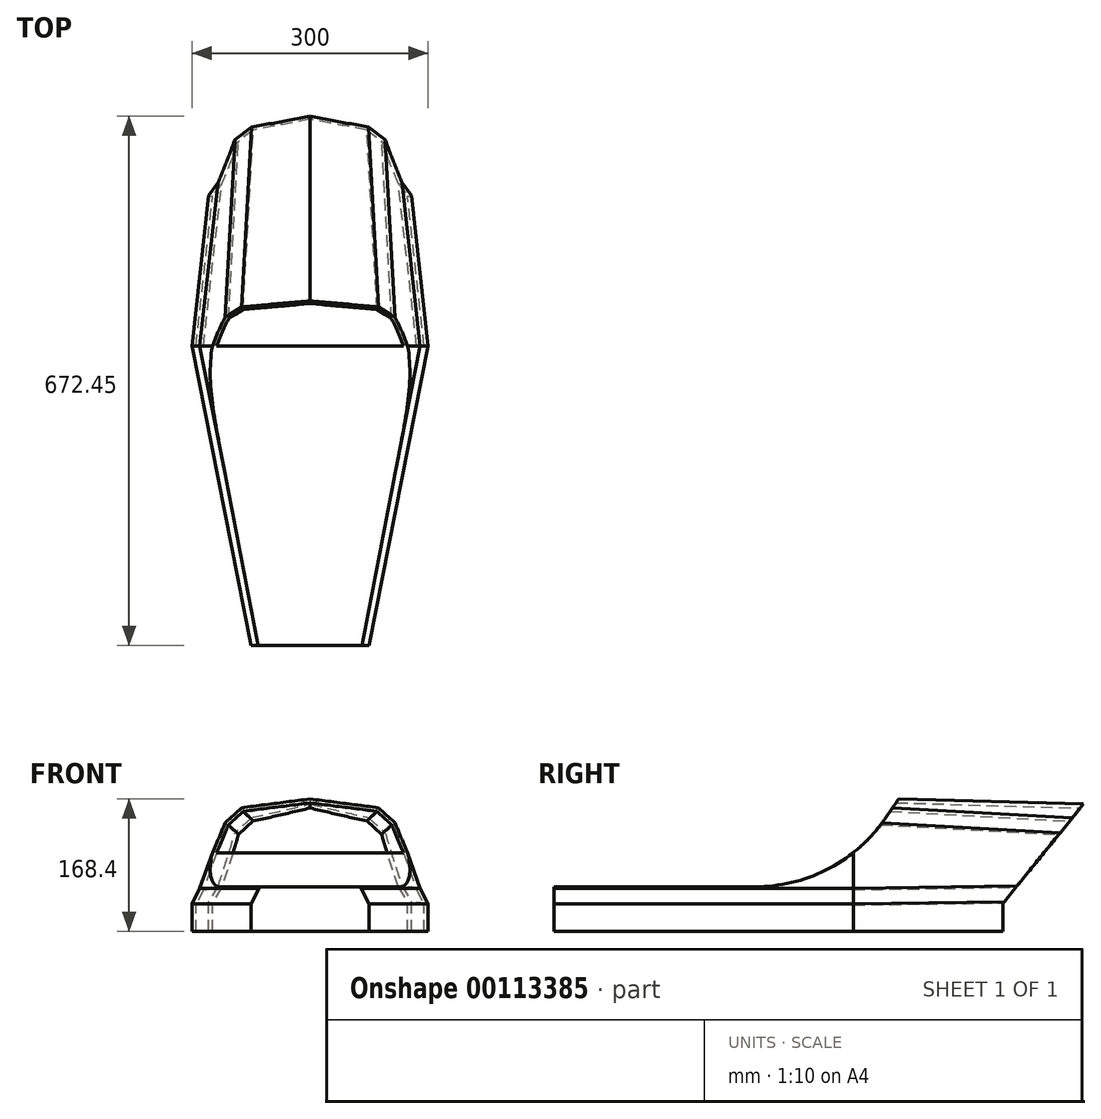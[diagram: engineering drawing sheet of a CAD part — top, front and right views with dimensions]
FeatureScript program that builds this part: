
annotation { "Feature Type Name" : "Feature", "Feature Type Description" : "" }
export const myFeature = defineFeature(function(context is Context, id is Id, definition is map)
    precondition{}
    {
        {
            var Q0;
            Q0=qCreatedBy(makeId("Front.planeOp"),FACE);
            cPlane(context, id + "F0", {"entities" : qUnion([Q0]), "cplaneType" : CPlaneType.OFFSET, "offset" : 360 * mm, "oppositeDirection" : true, "width" : 150 * mm, "height" : 150 * mm});
        }
        {
            var Q0;
            Q0=qCreatedBy(makeId("Front.planeOp"),FACE);
            cPlane(context, id + "F1", {"entities" : qUnion([Q0]), "cplaneType" : CPlaneType.OFFSET, "offset" : 380 * mm, "width" : 150 * mm, "height" : 150 * mm});
        }
        {
            var Q0;
            Q0=qCreatedBy(makeId("Front.planeOp"),FACE);
            var sketch = newSketch(context, id + "F2", { "sketchPlane" : qUnion([Q0])});
            skLineSegment(sketch, "E0", {"start": v(0, 0) * mm, "end": v(0, 170) * mm, "construction": true});
            skLineSegment(sketch, "E1", {"start": v(0, 0) * mm, "end": v(150, 0) * mm, "construction": true});
            skLineSegment(sketch, "E2", {"start": v(150, 0) * mm, "end": v(150, 35) * mm});
            skLineSegment(sketch, "E3", {"start": v(150, 35) * mm, "end": v(140, 35) * mm, "construction": true});
            skLineSegment(sketch, "E4", {"start": v(140, 35) * mm, "end": v(140, 55) * mm, "construction": true});
            skLineSegment(sketch, "E5", {"start": v(0, 170) * mm, "end": v(90, 170) * mm, "construction": true});
            skLineSegment(sketch, "E6", {"start": v(90, 170) * mm, "end": v(90, 160) * mm, "construction": true});
            skLineSegment(sketch, "E7", {"start": v(90, 160) * mm, "end": v(90, 140) * mm, "construction": true});
            skLineSegment(sketch, "E8", {"start": v(90, 140) * mm, "end": v(110, 140) * mm, "construction": true});
            skLineSegment(sketch, "E9", {"start": v(0, 170) * mm, "end": v(90, 160) * mm});
            skLineSegment(sketch, "E10", {"start": v(90, 160) * mm, "end": v(110, 140) * mm});
            skLineSegment(sketch, "E11", {"start": v(110, 140) * mm, "end": v(140, 55) * mm});
            skLineSegment(sketch, "E12", {"start": v(140, 55) * mm, "end": v(150, 35) * mm});
            skLineSegment(sketch, "E13.MirrorCS", {"start": v(-150, 0) * mm, "end": v(-150, 35) * mm});
            skLineSegment(sketch, "E14.MirrorCS", {"start": v(-140, 55) * mm, "end": v(-150, 35) * mm});
            skLineSegment(sketch, "E15.MirrorCS", {"start": v(-110, 140) * mm, "end": v(-140, 55) * mm});
            skLineSegment(sketch, "E16.MirrorCS", {"start": v(0, 170) * mm, "end": v(-90, 160) * mm});
            skLineSegment(sketch, "E17.MirrorCS", {"start": v(-90, 160) * mm, "end": v(-110, 140) * mm});
            skLineSegment(sketch, "E18.0", {"start": v(145, 0) * mm, "end": v(145, 33.82) * mm});
            skLineSegment(sketch, "E18.1", {"start": v(135.39, 53.04) * mm, "end": v(145, 33.82) * mm});
            skLineSegment(sketch, "E18.2", {"start": v(105.66, 137.27) * mm, "end": v(135.39, 53.04) * mm});
            skLineSegment(sketch, "E18.3", {"start": v(87.7, 155.22) * mm, "end": v(105.66, 137.27) * mm});
            skLineSegment(sketch, "E18.4", {"start": v(0, 164.97) * mm, "end": v(87.7, 155.22) * mm});
            skLineSegment(sketch, "E18.5", {"start": v(0, 164.97) * mm, "end": v(-87.7, 155.22) * mm});
            skLineSegment(sketch, "E18.6", {"start": v(-145, 0) * mm, "end": v(-145, 33.82) * mm});
            skLineSegment(sketch, "E18.7", {"start": v(-135.39, 53.04) * mm, "end": v(-145, 33.82) * mm});
            skLineSegment(sketch, "E18.8", {"start": v(-105.66, 137.27) * mm, "end": v(-135.39, 53.04) * mm});
            skLineSegment(sketch, "E18.9", {"start": v(-87.7, 155.22) * mm, "end": v(-105.66, 137.27) * mm});
            skLineSegment(sketch, "E19", {"start": v(-150, 0) * mm, "end": v(-145, 0) * mm});
            skLineSegment(sketch, "E20", {"start": v(145, 0) * mm, "end": v(150, 0) * mm});
            skSolve(sketch);
        }
        {
            var Q0;
            Q0=qCreatedBy(id+"F0.planeOp",FACE);
            var sketch = newSketch(context, id + "F3", { "sketchPlane" : qUnion([Q0])});
            skLineSegment(sketch, "E21", {"start": v(0, 0) * mm, "end": v(0, 160) * mm, "construction": true});
            skLineSegment(sketch, "E22", {"start": v(0, 0) * mm, "end": v(110, 0) * mm, "construction": true});
            skLineSegment(sketch, "E23", {"start": v(110, 0) * mm, "end": v(110, 40) * mm});
            skLineSegment(sketch, "E24", {"start": v(110, 40) * mm, "end": v(100, 40) * mm, "construction": true});
            skLineSegment(sketch, "E25", {"start": v(100, 40) * mm, "end": v(100, 60) * mm, "construction": true});
            skLineSegment(sketch, "E26", {"start": v(0, 160) * mm, "end": v(70, 160) * mm, "construction": true});
            skLineSegment(sketch, "E27", {"start": v(70, 160) * mm, "end": v(70, 140) * mm, "construction": true});
            skLineSegment(sketch, "E28", {"start": v(70, 140) * mm, "end": v(70, 120) * mm, "construction": true});
            skLineSegment(sketch, "E29", {"start": v(70, 120) * mm, "end": v(90, 120) * mm, "construction": true});
            skLineSegment(sketch, "E30", {"start": v(0, 160) * mm, "end": v(70, 140) * mm});
            skLineSegment(sketch, "E31", {"start": v(70, 140) * mm, "end": v(90, 120) * mm});
            skLineSegment(sketch, "E32", {"start": v(90, 120) * mm, "end": v(100, 60) * mm});
            skLineSegment(sketch, "E33", {"start": v(100, 60) * mm, "end": v(110, 40) * mm});
            skLineSegment(sketch, "E34.MirrorCS", {"start": v(-110, 0) * mm, "end": v(-110, 40) * mm});
            skLineSegment(sketch, "E35.MirrorCS", {"start": v(-100, 60) * mm, "end": v(-110, 40) * mm});
            skLineSegment(sketch, "E36.MirrorCS", {"start": v(-90, 120) * mm, "end": v(-100, 60) * mm});
            skLineSegment(sketch, "E37.MirrorCS", {"start": v(0, 160) * mm, "end": v(-70, 140) * mm});
            skLineSegment(sketch, "E38.MirrorCS", {"start": v(-70, 140) * mm, "end": v(-90, 120) * mm});
            skLineSegment(sketch, "E39.0", {"start": v(105, 0) * mm, "end": v(105, 38.82) * mm});
            skLineSegment(sketch, "E39.1", {"start": v(95.2, 58.44) * mm, "end": v(105, 38.82) * mm});
            skLineSegment(sketch, "E39.2", {"start": v(85.33, 117.6) * mm, "end": v(95.2, 58.44) * mm});
            skLineSegment(sketch, "E39.3", {"start": v(67.38, 135.55) * mm, "end": v(85.33, 117.6) * mm});
            skLineSegment(sketch, "E39.4", {"start": v(0, 154.8) * mm, "end": v(67.38, 135.55) * mm});
            skLineSegment(sketch, "E39.5", {"start": v(0, 154.8) * mm, "end": v(-67.38, 135.55) * mm});
            skLineSegment(sketch, "E39.6", {"start": v(-105, 0) * mm, "end": v(-105, 38.82) * mm});
            skLineSegment(sketch, "E39.7", {"start": v(-95.2, 58.44) * mm, "end": v(-105, 38.82) * mm});
            skLineSegment(sketch, "E39.8", {"start": v(-85.33, 117.6) * mm, "end": v(-95.2, 58.44) * mm});
            skLineSegment(sketch, "E39.9", {"start": v(-67.38, 135.55) * mm, "end": v(-85.33, 117.6) * mm});
            skLineSegment(sketch, "E40", {"start": v(-110, 0) * mm, "end": v(-105, 0) * mm});
            skLineSegment(sketch, "E41", {"start": v(110, 0) * mm, "end": v(105, 0) * mm});
            skSolve(sketch);
        }
        {
            var Q0;
            Q0=makeQuery(id+"F2.imprint","IMPRINT",FACE,{"disambiguationData":[TD([[makeQuery(id+"F2.imprint","IMPRINT",EDGE,{"derivedFrom":sQuery(id+"F2.wireOp",EDGE,"E2")}),1.0]])]});
            var Q1;
            Q1=makeQuery(id+"F3.imprint","IMPRINT",FACE,{"disambiguationData":[TD([[makeQuery(id+"F3.imprint","IMPRINT",EDGE,{"derivedFrom":sQuery(id+"F3.wireOp",EDGE,"E23")}),1.0]])]});
            loft(context, id + "F4", {"sheetProfilesArray" : [{ "sheetProfileEntities" : qUnion([Q0]) }, { "sheetProfileEntities" : qUnion([Q1]) }]});
        }
        {
            var Q0;
            Q0=qCreatedBy(makeId("Right.planeOp"),FACE);
            var sketch = newSketch(context, id + "F5", { "sketchPlane" : qUnion([Q0])});
            skLineSegment(sketch, "E42", {"start": v(0, 0) * mm, "end": v(190, 0) * mm, "construction": true});
            skLineSegment(sketch, "E43", {"start": v(190, 0) * mm, "end": v(190, 35.57) * mm});
            skLineSegment(sketch, "E44", {"start": v(190, 35.57) * mm, "end": v(299.22, 170.23) * mm});
            skLineSegment(sketch, "E45", {"start": v(299.22, 170.23) * mm, "end": v(363.76, 190.56) * mm});
            skLineSegment(sketch, "E46", {"start": v(363.76, 190.56) * mm, "end": v(429.83, 105.19) * mm});
            skLineSegment(sketch, "E47", {"start": v(429.83, 105.19) * mm, "end": v(427.62, -24.65) * mm});
            skLineSegment(sketch, "E48", {"start": v(427.62, -24.65) * mm, "end": v(17.26, -21.49) * mm});
            skLineSegment(sketch, "E49", {"start": v(17.26, -21.49) * mm, "end": v(189.97, -2.04) * mm});
            skLineSegment(sketch, "E50", {"start": v(189.97, -2.04) * mm, "end": v(190, 0) * mm});
            skSolve(sketch);
        }
        {
            var Q0;
            Q0=makeQuery(id+"F5.imprint","IMPRINT",FACE,{"disambiguationData":[TD([[makeQuery(id+"F5.imprint","IMPRINT",EDGE,{"derivedFrom":sQuery(id+"F5.wireOp",EDGE,"Y5QNh29d-IWdV-9vjP-PHoZ-EMxwuHQiGpys")}),-1.0]])]});
            var Q1;
            Q1=makeQuery(id+"F5.imprint","IMPRINT",FACE,{"disambiguationData":[TD([[makeQuery(id+"F5.imprint","IMPRINT",EDGE,{"derivedFrom":sQuery(id+"F5.wireOp",EDGE,"E43")}),-1.0]])]});
            extrude(context, id + "F6", {"entities" : qUnion([Q0, Q1]), "operationType" : NewBodyOperationType.REMOVE, "endBound" : BoundingType.SYMMETRIC, "depth" : 300 * mm});
        }
        {
            var Q0;
            Q0=qCreatedBy(id+"F1.planeOp",FACE);
            var sketch = newSketch(context, id + "F7", { "sketchPlane" : qUnion([Q0])});
            skLineSegment(sketch, "E51", {"start": v(0, 0) * mm, "end": v(0, 160) * mm, "construction": true});
            skLineSegment(sketch, "E52", {"start": v(0, 0) * mm, "end": v(75, 0) * mm, "construction": true});
            skLineSegment(sketch, "E53", {"start": v(75, 0) * mm, "end": v(75, 35) * mm});
            skLineSegment(sketch, "E54", {"start": v(75, 35) * mm, "end": v(65, 35) * mm, "construction": true});
            skLineSegment(sketch, "E55", {"start": v(65, 35) * mm, "end": v(65, 55) * mm, "construction": true});
            skLineSegment(sketch, "E56", {"start": v(0, 160) * mm, "end": v(90, 160) * mm, "construction": true});
            skLineSegment(sketch, "E57", {"start": v(90, 160) * mm, "end": v(90, 150) * mm, "construction": true});
            skLineSegment(sketch, "E58", {"start": v(90, 150) * mm, "end": v(90, 130) * mm, "construction": true});
            skLineSegment(sketch, "E59", {"start": v(90, 130) * mm, "end": v(110, 130) * mm, "construction": true});
            skLineSegment(sketch, "E60", {"start": v(0, 160) * mm, "end": v(90, 150) * mm});
            skLineSegment(sketch, "E61", {"start": v(90, 150) * mm, "end": v(110, 130) * mm});
            skLineSegment(sketch, "E62", {"start": v(110, 130) * mm, "end": v(65, 55) * mm});
            skLineSegment(sketch, "E63", {"start": v(65, 55) * mm, "end": v(75, 35) * mm});
            skLineSegment(sketch, "E64.MirrorCS", {"start": v(-75, 0) * mm, "end": v(-75, 35) * mm});
            skLineSegment(sketch, "E65.MirrorCS", {"start": v(-65, 55) * mm, "end": v(-75, 35) * mm});
            skLineSegment(sketch, "E66.MirrorCS", {"start": v(-110, 130) * mm, "end": v(-65, 55) * mm});
            skLineSegment(sketch, "E67.MirrorCS", {"start": v(0, 160) * mm, "end": v(-90, 150) * mm});
            skLineSegment(sketch, "E68.MirrorCS", {"start": v(-90, 150) * mm, "end": v(-110, 130) * mm});
            skLineSegment(sketch, "E69", {"start": v(-75, 0) * mm, "end": v(75, 0) * mm});
            skSolve(sketch);
        }
        {
            var Q0;
            Q0=qCreatedBy(makeId("Front.planeOp"),FACE);
            var sketch = newSketch(context, id + "F8", { "sketchPlane" : qUnion([Q0])});
            skLineSegment(sketch, "E70", {"start": v(0, 0) * mm, "end": v(0, 170) * mm, "construction": true});
            skLineSegment(sketch, "E71", {"start": v(0, 0) * mm, "end": v(150, 0) * mm, "construction": true});
            skLineSegment(sketch, "E72", {"start": v(150, 0) * mm, "end": v(150, 35) * mm});
            skLineSegment(sketch, "E73", {"start": v(150, 35) * mm, "end": v(140, 35) * mm, "construction": true});
            skLineSegment(sketch, "E74", {"start": v(140, 35) * mm, "end": v(140, 55) * mm, "construction": true});
            skLineSegment(sketch, "E75", {"start": v(0, 170) * mm, "end": v(90, 170) * mm, "construction": true});
            skLineSegment(sketch, "E76", {"start": v(90, 170) * mm, "end": v(90, 160) * mm, "construction": true});
            skLineSegment(sketch, "E77", {"start": v(90, 160) * mm, "end": v(90, 140) * mm, "construction": true});
            skLineSegment(sketch, "E78", {"start": v(90, 140) * mm, "end": v(110, 140) * mm, "construction": true});
            skLineSegment(sketch, "E79", {"start": v(0, 170) * mm, "end": v(90, 160) * mm});
            skLineSegment(sketch, "E80", {"start": v(90, 160) * mm, "end": v(110, 140) * mm});
            skLineSegment(sketch, "E81", {"start": v(110, 140) * mm, "end": v(140, 55) * mm});
            skLineSegment(sketch, "E82", {"start": v(140, 55) * mm, "end": v(150, 35) * mm});
            skLineSegment(sketch, "E83.MirrorCS", {"start": v(-150, 0) * mm, "end": v(-150, 35) * mm});
            skLineSegment(sketch, "E84.MirrorCS", {"start": v(-140, 55) * mm, "end": v(-150, 35) * mm});
            skLineSegment(sketch, "E85.MirrorCS", {"start": v(-110, 140) * mm, "end": v(-140, 55) * mm});
            skLineSegment(sketch, "E86.MirrorCS", {"start": v(0, 170) * mm, "end": v(-90, 160) * mm});
            skLineSegment(sketch, "E87.MirrorCS", {"start": v(-90, 160) * mm, "end": v(-110, 140) * mm});
            skLineSegment(sketch, "E88", {"start": v(-150, 0) * mm, "end": v(150, 0) * mm});
            skSolve(sketch);
        }
        {
            var Q1;
            Q1=makeQuery(id+"F8.imprint","IMPRINT",FACE,{"disambiguationData":[TD([[makeQuery(id+"F8.imprint","IMPRINT",EDGE,{"derivedFrom":sQuery(id+"F8.wireOp",EDGE,"E72")}),1.0]])]});
            var Q2;
            Q2=makeQuery(id+"F7.imprint","IMPRINT",FACE,{"disambiguationData":[TD([[makeQuery(id+"F7.imprint","IMPRINT",EDGE,{"derivedFrom":sQuery(id+"F7.wireOp",EDGE,"E53")}),1.0]])]});
            loft(context, id + "F9", {"operationType" : NewBodyOperationType.ADD, "sheetProfilesArray" : [{ "sheetProfileEntities" : qUnion([Q1]) }, { "sheetProfileEntities" : qUnion([Q2]) }]});
        }
        {
            var Q0;
            Q0=qCreatedBy(makeId("Right.planeOp"),FACE);
            var sketch = newSketch(context, id + "F10", { "sketchPlane" : qUnion([Q0])});
            skLineSegment(sketch, "E89", {"start": v(80.78, 1.8) * mm, "end": v(80.78, 201.8) * mm, "construction": true});
            skLineSegment(sketch, "E90", {"start": v(80.78, 1.8) * mm, "end": v(-299.22, 1.8) * mm, "construction": true});
            skLineSegment(sketch, "E91", {"start": v(80.78, 56.8) * mm, "end": v(-19.22, 56.8) * mm, "construction": true});
            skLineSegment(sketch, "E92", {"start": v(80.78, 56.8) * mm, "end": v(-388.36, 56.8) * mm});
            skPoint(sketch, "E92.endSnap0", {"position": v(30.78, 56.8) * mm});
            skLineSegment(sketch, "E93", {"start": v(80.78, 201.8) * mm, "end": v(40.4, 143.26) * mm});
            skLineSegment(sketch, "E94", {"start": v(-124.24, 56.8) * mm, "end": v(-388.36, 56.8) * mm});
            skPoint(sketch, "E95.visualSharp", {"position": v(-19.22, 56.8) * mm});
            skArc(sketch, "E95.filletArc", {"start": v(-124.24, 56.8) * mm, "mid": v(-31.26, 79.73) * mm, "end": v(40.4, 143.26) * mm});
            skLineSegment(sketch, "E96", {"start": v(-388.36, 56.8) * mm, "end": v(-388.36, 199.96) * mm});
            skLineSegment(sketch, "E97", {"start": v(-388.36, 199.96) * mm, "end": v(45.38, 256.79) * mm});
            skLineSegment(sketch, "E98", {"start": v(45.38, 256.79) * mm, "end": v(80.78, 201.8) * mm});
            skSolve(sketch);
        }
        {
            var Q0;
            {var subQ5=sQuery(id+"F10.wireOp",EDGE,"qWPuRZU9-msRR-xt7t-3FR7-fbN9VGAxtSkB");Q0=makeQuery(id+"F10.imprint","IMPRINT",FACE,{"disambiguationData":[TD([[makeQuery(id+"F10.imprint","IMPRINT",EDGE,{"derivedFrom":subQ5}),1.0]])]});}
            var Q1;
            {var subQ5=sQuery(id+"F10.wireOp",EDGE,"lCp5wgT7-I75v-Bs02-0Fc4-qaaeCi8UGHWA");Q1=makeQuery(id+"F10.imprint","IMPRINT",FACE,{"disambiguationData":[TD([[makeQuery(id+"F10.imprint","IMPRINT",EDGE,{"derivedFrom":subQ5}),-1.0]])]});}
            var Q2;
            {var subQ5=sQuery(id+"F10.wireOp",EDGE,"qWPuRZU9-msRR-xt7t-3FR7-fbN9VGAxtSkB");Q2=makeQuery(id+"F10.imprint","IMPRINT",FACE,{"disambiguationData":[TD([[makeQuery(id+"F10.imprint","IMPRINT",EDGE,{"derivedFrom":subQ5}),-1.0]])]});}
            var Q3;
            Q3=makeQuery(id+"F10.imprint","IMPRINT",FACE,{"disambiguationData":[TD([[makeQuery(id+"F10.imprint","IMPRINT",EDGE,{"derivedFrom":sQuery(id+"F10.wireOp",EDGE,"FYUMeG4K-dbKx-ijqG-AGho-ki0m3fqrATME")}),-1.0]])]});
            var Q4;
            Q4=makeQuery(id+"F10.imprint","IMPRINT",FACE,{"disambiguationData":[TD([[makeQuery(id+"F10.imprint","IMPRINT",EDGE,{"derivedFrom":sQuery(id+"F10.wireOp",EDGE,"E93")}),-1.0]])]});
            extrude(context, id + "F11", {"entities" : qUnion([Q0, Q1, Q2, Q3, Q4]), "operationType" : NewBodyOperationType.REMOVE, "endBound" : BoundingType.SYMMETRIC, "oppositeDirection" : true, "depth" : 300 * mm});
        }
    });
